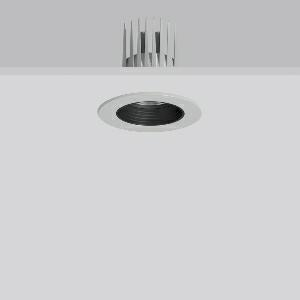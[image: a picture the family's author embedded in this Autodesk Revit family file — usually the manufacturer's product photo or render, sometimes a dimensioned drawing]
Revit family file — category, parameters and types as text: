
# Revit family: heledon_mini_e_901747_004_bff8
name_source: partatom
category: Lighting Fixtures
units: mm (PartAtom-declared; Revit-internal decimal feet)

## family parameters
Cut with Voids When Loaded = No
Host = Face
Light Source = No
Part Type = Normal
Room Calculation Point = No
Round Connector Dimension = Use Diameter
Shared = No

## types (1)
- HELEDON mini E (1 x LED Modul 930, 1950 lm, 3000)
    Apparent Load = 20 VA
    Approval mark = CE
    CIE Flux Codes = 95 100 100 100 100
    Color Rendering = 90
    Color Temperature = 3000
    Default Elevation = 1800 mm
    Description = Series: HELEDON mini
Round recessed downlight. Housing: die-cast aluminium, powder-coated. Black plastic ring and recessed LED to prevent glare from the side. Optical assembly with lens made of plastic (polycarbonate) for the best homogeneous light distribution - can be changed without tools. Best colour rendering index Ra>90. Suitable for Recessed ceiling mounting. Installation without tools thanks to spring fastening system. Including separate LED converter with connecting cable 600 mm.High quality converter without flickering and stroboscopic effect. Through-wiring box (5 pole) available as accessory. The following accessories can be mounted without use of tools: interchangeable lenses, decorative glasses, honeycomb louvre, clear and frosted diffusers, white interchangeable plastic ring. 
Colour: silver
Diameter: 124 mm
Height: 3 mm
Cut-out diameter: 114 mm
Recess height: 170 mm
Luminaire: recess height: 120 mm
Lamp: LED
Socket: without socket
Colour temperature: 3000K
Colour rendering index (CRI): 92
System power: 20 W
Rated luminous flux: 1950 lm
Luminous efficiency: 98 lm/W
Control gear: Regulated power supply
Protection class: II
Type of protection: IP 20
    Height = 0 mm  [stored 0 ft]
    Lamp = 1 x LED Modul 930
    Lamp Light Flux = 1950 lm
    Lamp count = 1
    Length = 124 mm  [stored 0.406824 ft]
    Lifetime = 50000 h
    Luminous efficacy = 98 lm/W
    Manufacturer = RZB
    ModVariant = No
    Model = 901747.004
    Mounting Place = Ceiling
    Mounting Type = Recessed
    Number of Poles = 1
    OnlyDefault = Yes
    Power Factor = 1
    Product Name = HELEDON mini E
    Product group = Recessed downlights
    ProductGroupID = 402
    Protection Class = Protection class II
    Protection Degree = IP 20
    RLX_Detail_Level = 1
    RLX_Emergency_Light_Flux = 0 lm
    RLX_Emergency_Type = 0
    RLX_Emergency_Type_DB = No
    RlxData = <blob elided: 133433 chars, md5=80fc0f2b>
    Socket = socket
    Standby Power = 0 W
    System Light Flux = 1950 lm
    System Power = 20 W
    Type Comments = Product without accessories
    Type Image = 901656.004.jpg
    URL = http://relux.com
    VarID = ---
    Voltage = 230 V
    Voltage Range = 220-240 V
    Weight = 0.00 kg
    Width = 0 mm  [stored 0 ft]

note: [stored X ft] marks values corroborated as IEEE doubles in the binary element streams (Revit-internal decimal feet)

## geometry (parser evidence)
native form markers: Blend x4, Sweep x9
no freeform markers — native parametric forms only
